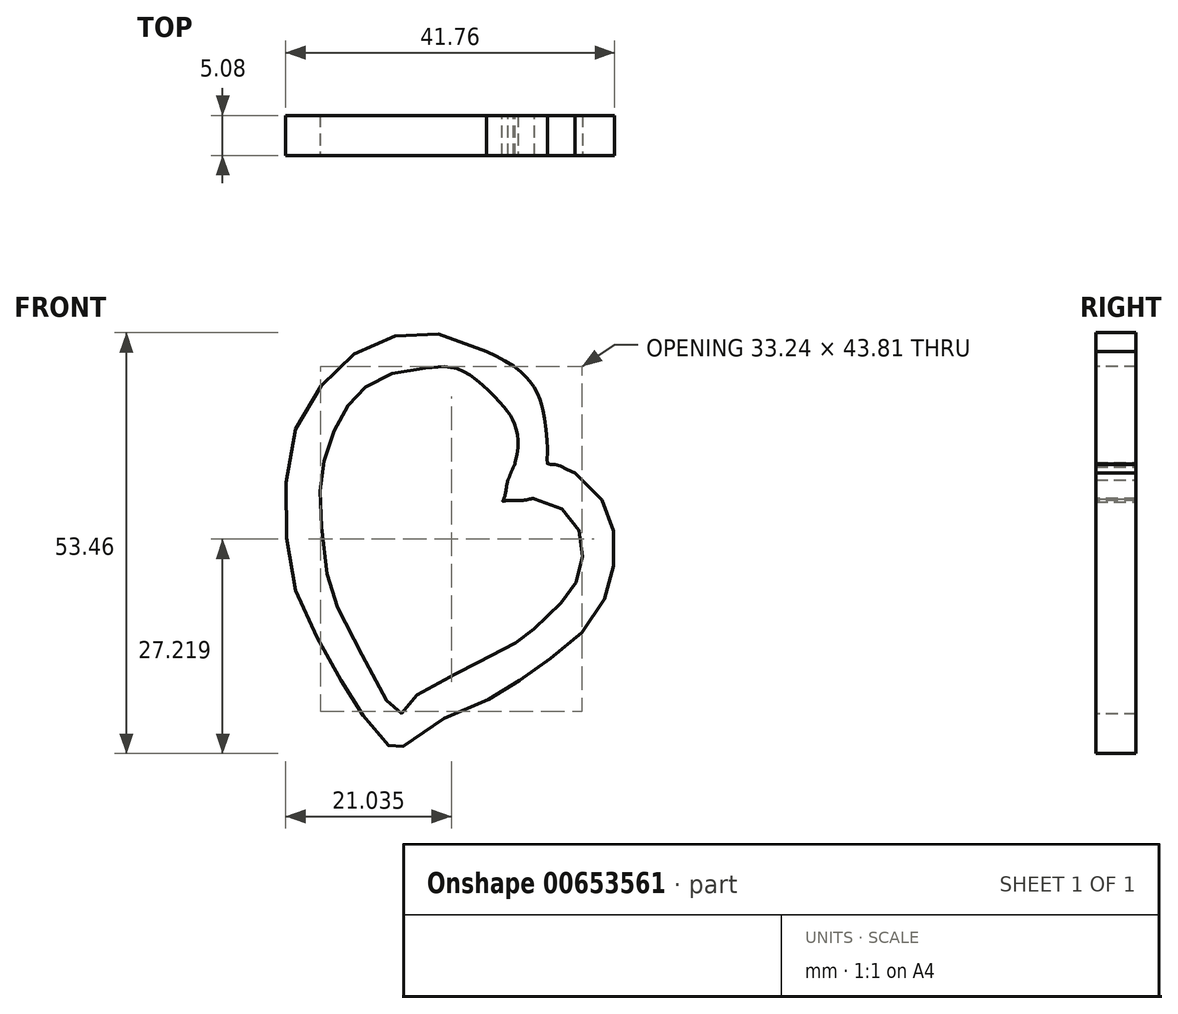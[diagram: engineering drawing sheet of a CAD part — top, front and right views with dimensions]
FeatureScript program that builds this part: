
annotation { "Feature Type Name" : "Feature", "Feature Type Description" : "" }
export const myFeature = defineFeature(function(context is Context, id is Id, definition is map)
    precondition{}
    {
        {
            var Q0;
            Q0=qCreatedBy(makeId("Front.planeOp"),FACE);
            var sketch = newSketch(context, id + "F0", { "sketchPlane" : qUnion([Q0])});
            skFitSpline(sketch, "E0", {"points": [v(-1.8, -4.47) * mm, v(-5.03, -3.66) * mm, v(-7.9, -1.06) * mm, v(-9.34, 3.24) * mm, v(-8.26, 7.55) * mm, v(-5.4, 10.42) * mm, v(0, 8.9) * mm, v(-1.09, 4.32) * mm, v(-2.52, 3.42) * mm, v(-5.4, 3.87) * mm, v(-6.47, 2.8) * mm, v(-3.6, 0) * mm, v(-1.76, -0.47) * mm, v(-2.24, -2.36) * mm, v(-1.8, -4.47) * mm]});
            skFitSpline(sketch, "E1", {"points": [v(1.67, -4.47) * mm, v(5.07, -3.84) * mm, v(8.11, -1.69) * mm, v(10.78, 1.65) * mm, v(11.6, 3.78) * mm, v(10.66, 3.69) * mm, v(8.93, 3.6) * mm, v(7.47, 3.41) * mm, v(5.96, 1.86) * mm, v(4.2, 0.4) * mm, v(2.25, -0.44) * mm, v(1.89, -1.63) * mm, v(1.67, -4.47) * mm]});
            skFitSpline(sketch, "E2", {"points": [v(-1.8, -4.47) * mm, v(-2.15, -5.12) * mm, v(-1.8, -6.81) * mm, v(-0.44, -9.45) * mm, v(1.42, -11.73) * mm, v(5.96, -13.24) * mm, v(9.17, -12.7) * mm, v(11.61, -10.7) * mm, v(13.06, -7.91) * mm, v(11.8, -6.2) * mm, v(9.68, -3.56) * mm, v(7.19, -3.95) * mm, v(5.62, -5.64) * mm, v(3.76, -7.81) * mm, v(2.52, -7.91) * mm, v(2.2, -5.9) * mm, v(1.95, -4.64) * mm, v(-1.8, -4.47) * mm]});
            skFitSpline(sketch, "E3", {"points": [v(-1.76, -0.47) * mm, v(-0.48, 2.09) * mm, v(2.16, 5.26) * mm, v(5.85, 7.9) * mm, v(9.1, 8.42) * mm, v(8.42, 6.95) * mm, v(7.47, 3.41) * mm, v(5.85, 3.07) * mm, v(4.04, 1.71) * mm, v(3.15, 0) * mm, v(-1.76, -0.47) * mm]});
            skFitSpline(sketch, "E4", {"points": [v(12.94, 7.97) * mm, v(16.71, 7.07) * mm, v(20.03, 3.82) * mm, v(21.43, 0.58) * mm, v(21.73, -3.27) * mm, v(21.16, -6.81) * mm, v(19.58, -10.73) * mm, v(15.72, -14.94) * mm, v(11.88, -17.66) * mm, v(8.23, -20.28) * mm, v(4.3, -22.34) * mm, v(-3.5, -26.18) * mm, v(-6.17, -28.55) * mm, v(-6.52, -28.14) * mm, v(-9.2, -25) * mm, v(-12.1, -20.87) * mm, v(-15.6, -14.65) * mm, v(-19.08, -6.81) * mm, v(-20.01, 2.33) * mm, v(-19.03, 11.82) * mm, v(-15.02, 18.74) * mm, v(-10.18, 22.89) * mm, v(-4.1, 24.83) * mm, v(2.25, 24) * mm, v(9.88, 19.57) * mm, v(12.1, 15.7) * mm, v(12.94, 7.97) * mm]});
            skPoint(sketch, "E5.1.internal.orphan", {"position": v(9.1, 13.2) * mm});
            skPoint(sketch, "E5.16.internal.orphan", {"position": v(-5.03, -23.28) * mm});
            skPoint(sketch, "E5.17.internal.orphan", {"position": v(-3.5, -21.3) * mm});
            skPoint(sketch, "E5.2.internal.orphan", {"position": v(7.47, 15.7) * mm});
            skPoint(sketch, "E5.25.internal.orphan", {"position": v(17.59, -2.36) * mm});
            skPoint(sketch, "E5.3.internal.orphan", {"position": v(2.25, 20.12) * mm});
            skPoint(sketch, "E5.4.internal.orphan", {"position": v(-2.24, 20.4) * mm});
            skFitSpline(sketch, "E6", {"points": [v(5.47, 22.5) * mm, v(8.65, 20.83) * mm, v(10.48, 19.3) * mm, v(11.34, 18.25) * mm, v(12.17, 16.7) * mm, v(12.5, 15.7) * mm, v(12.87, 13.92) * mm, v(13.2, 10.35) * mm, v(13.2, 9.52) * mm, v(13.18, 8.4) * mm, v(13.28, 8.2) * mm, v(13.89, 8.2) * mm, v(14.8, 7.97) * mm, v(16.71, 7.07) * mm], "startDerivative": vector(28.37, -13) * mm, "endDerivative": vector(22.84, -11.32) * mm});
            skFitSpline(sketch, "E7", {"points": [v(8.65, 8.54) * mm, v(8.68, 9.36) * mm, v(8.56, 12.3) * mm, v(7.19, 14.76) * mm, v(5.33, 17.06) * mm, v(2.26, 19.16) * mm, v(0, 19.92) * mm, v(-2.24, 20.4) * mm], "startDerivative": vector(0.16, 8.13) * mm, "endDerivative": vector(-16.54, 3.36) * mm});
            skFitSpline(sketch, "E8.trimOffspring", {"points": [v(9.1, 8.42) * mm, v(9.1, 13.2) * mm, v(7.47, 15.7) * mm, v(2.25, 20.12) * mm, v(-2.24, 20.4) * mm, v(-6.8, 19.66) * mm, v(-9.84, 18.02) * mm, v(-11.71, 16.2) * mm, v(-13.35, 13.52) * mm, v(-14.7, 10.2) * mm, v(-15.55, 6.08) * mm, v(-15.6, 2.61) * mm, v(-14.76, -5.78) * mm, v(-13.14, -10.64) * mm, v(-7.63, -21.09) * mm, v(-5.93, -23.46) * mm, v(-5.03, -23.28) * mm, v(-3.5, -21.3) * mm, v(2.51, -18) * mm, v(4.06, -17.14) * mm, v(9.77, -14.21) * mm, v(10.92, -13.36) * mm, v(14.68, -9.77) * mm, v(16.4, -7.66) * mm, v(17.54, -4.88) * mm, v(17.59, -2.36) * mm, v(16.98, 0.46) * mm, v(14.83, 2.7) * mm, v(11.6, 3.78) * mm, v(7.47, 3.41) * mm, v(9.1, 8.42) * mm]});
            skFitSpline(sketch, "E9", {"points": [v(2.31, -0.4) * mm, v(2.31, -0.18) * mm, v(2.5, 0.18) * mm, v(2.84, 0.63) * mm, v(3.29, 1.17) * mm, v(3.66, 1.63) * mm, v(4.33, 2.3) * mm, v(4.6, 2.56) * mm, v(4.86, 2.74) * mm, v(5.35, 3) * mm, v(5.75, 3.16) * mm, v(6.39, 3.34) * mm, v(6.84, 3.4) * mm, v(7.28, 3.37) * mm, v(7.19, 3.23) * mm], "startDerivative": vector(-0.55, 4.19) * mm, "endDerivative": vector(-3.87, -3.94) * mm});
            skSolve(sketch);
        }
        {
            var Q0;
            Q0 = qSketchRegion(id + "F0", true);
            extrude(context, id + "F1", {"entities" : qUnion([Q0]), "depth" : 5.08 * mm, "offsetDistance" : 25.4 * mm});
        }
    });
